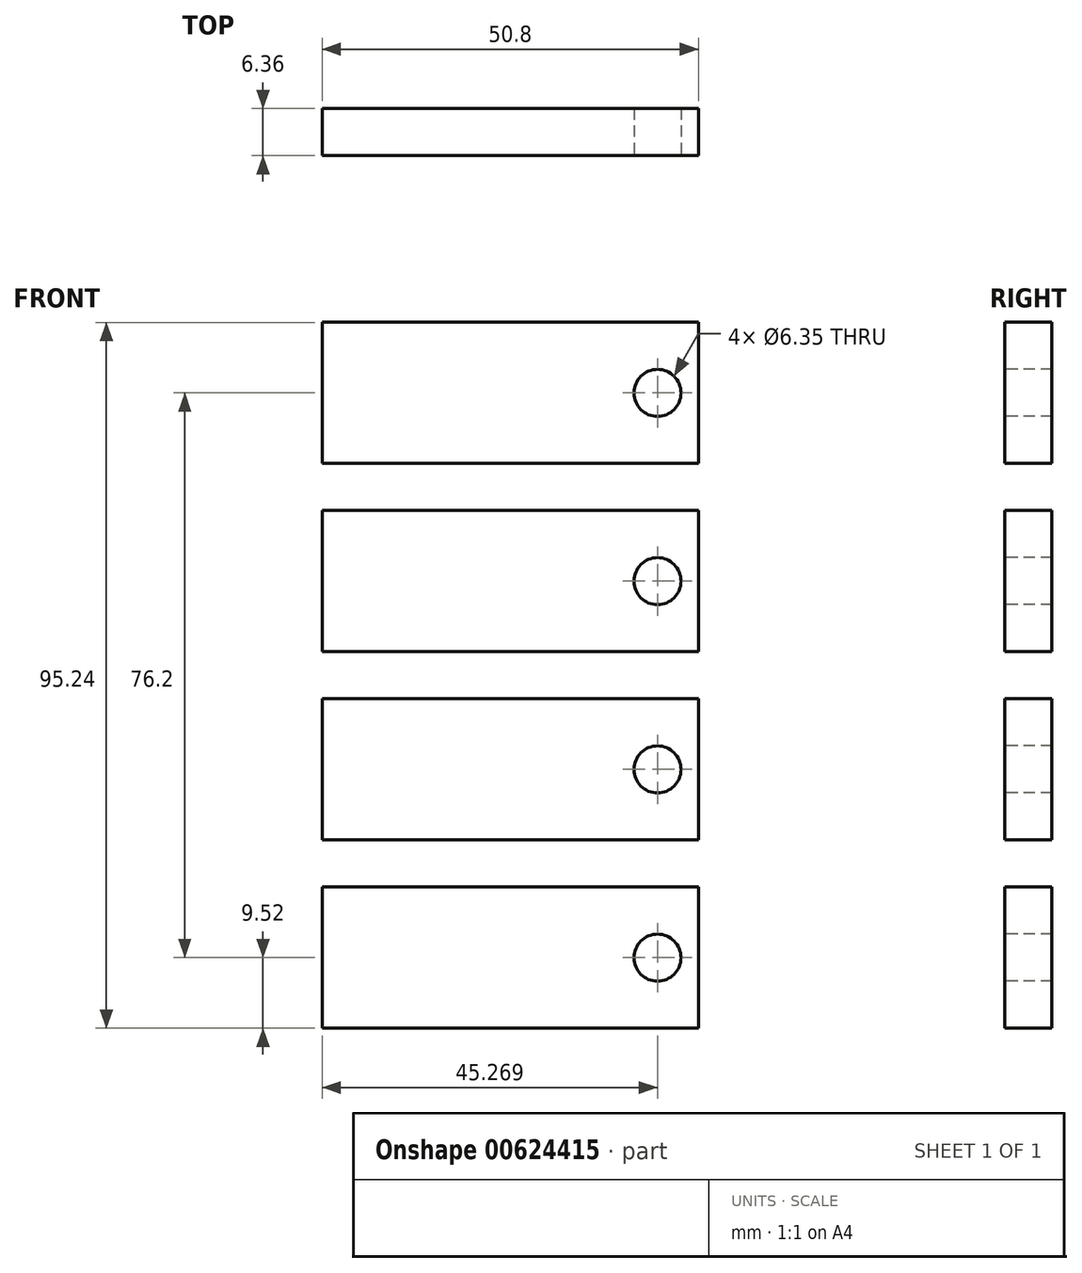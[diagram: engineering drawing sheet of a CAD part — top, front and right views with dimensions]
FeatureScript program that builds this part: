
annotation { "Feature Type Name" : "Feature", "Feature Type Description" : "" }
export const myFeature = defineFeature(function(context is Context, id is Id, definition is map)
    precondition{}
    {
        {
            var Q0;
            Q0=qCreatedBy(makeId("Front.planeOp"),FACE);
            var sketch = newSketch(context, id + "F0", { "sketchPlane" : qUnion([Q0])});
            skLineSegment(sketch, "E0.bottom", {"start": v(-25.4, -9.53) * mm, "end": v(25.4, -9.53) * mm});
            skLineSegment(sketch, "E0.top", {"start": v(-25.4, 9.53) * mm, "end": v(25.4, 9.53) * mm});
            skLineSegment(sketch, "E0.left", {"start": v(-25.4, -9.53) * mm, "end": v(-25.4, 9.53) * mm});
            skLineSegment(sketch, "E0.right", {"start": v(25.4, -9.53) * mm, "end": v(25.4, 9.53) * mm});
            skPoint(sketch, "E0.middle", {"position": v(0, 0) * mm});
            skLineSegment(sketch, "E1.bottom", {"start": v(-25.4, 15.88) * mm, "end": v(25.4, 15.88) * mm});
            skLineSegment(sketch, "E1.top", {"start": v(-25.4, 34.93) * mm, "end": v(25.4, 34.93) * mm});
            skLineSegment(sketch, "E1.left", {"start": v(-25.4, 15.88) * mm, "end": v(-25.4, 34.93) * mm});
            skLineSegment(sketch, "E1.right", {"start": v(25.4, 15.88) * mm, "end": v(25.4, 34.93) * mm});
            skPoint(sketch, "E1.middle", {"position": v(0, 25.4) * mm});
            skPoint(sketch, "E1.cornerSnap0", {"position": v(-25.4, 0) * mm});
            skLineSegment(sketch, "E2.bottom", {"start": v(-25.4, -34.92) * mm, "end": v(25.4, -34.92) * mm});
            skLineSegment(sketch, "E2.top", {"start": v(-25.4, -15.88) * mm, "end": v(25.4, -15.88) * mm});
            skLineSegment(sketch, "E2.left", {"start": v(-25.4, -34.93) * mm, "end": v(-25.4, -15.88) * mm});
            skLineSegment(sketch, "E2.right", {"start": v(25.4, -34.92) * mm, "end": v(25.4, -15.88) * mm});
            skPoint(sketch, "E2.middle", {"position": v(0, -25.4) * mm});
            skLineSegment(sketch, "E3.bottom", {"start": v(-25.4, -60.33) * mm, "end": v(25.4, -60.33) * mm});
            skLineSegment(sketch, "E3.top", {"start": v(-25.4, -41.28) * mm, "end": v(25.4, -41.28) * mm});
            skLineSegment(sketch, "E3.left", {"start": v(-25.4, -60.33) * mm, "end": v(-25.4, -41.28) * mm});
            skLineSegment(sketch, "E3.right", {"start": v(25.4, -60.33) * mm, "end": v(25.4, -41.28) * mm});
            skPoint(sketch, "E3.middle", {"position": v(0, -50.8) * mm});
            skSolve(sketch);
        }
        {
            var Q0;
            Q0 = qSketchRegion(id + "F0", true);
            extrude(context, id + "F1", {"entities" : qUnion([Q0]), "endBound" : BoundingType.SYMMETRIC, "depth" : 6.35 * mm, "offsetDistance" : 25.4 * mm});
        }
        {
            var Q0;
            Q0=makeQuery(id+"F1.opExtrude","CAP_FACE",FACE,{"disambiguationData":[OSD([sQuery(id+"F0.wireOp",EDGE,"E1.bottom"),sQuery(id+"F0.wireOp",EDGE,"E1.top"),sQuery(id+"F0.wireOp",EDGE,"E1.left"),sQuery(id+"F0.wireOp",EDGE,"E1.right")])],"isStart":false});
            var sketch = newSketch(context, id + "F2", { "sketchPlane" : qUnion([Q0])});
            skCircle(sketch, "E4", {"center": v(19.87, 25.4) * mm, "radius": 3.26 * mm});
            skPoint(sketch, "E4.centerSnap0", {"position": v(25.4, 25.4) * mm});
            skCircle(sketch, "E5", {"center": v(19.87, 0) * mm, "radius": 3.05 * mm});
            skCircle(sketch, "E6", {"center": v(19.87, -25.4) * mm, "radius": 3.05 * mm});
            skCircle(sketch, "E7", {"center": v(19.87, -50.8) * mm, "radius": 2.7 * mm});
            skSolve(sketch);
        }
        {
            var Q0;
            Q0=sQuery(id+"F2.wireOp",VERTEX,"E4.center");
            var Q1;
            Q1=sQuery(id+"F2.wireOp",VERTEX,"E5.center");
            var Q2;
            Q2=sQuery(id+"F2.wireOp",VERTEX,"E6.center");
            var Q3;
            Q3=sQuery(id+"F2.wireOp",VERTEX,"E7.center");
            var Q4;
            Q4=makeQuery(id+"F1.opExtrude","SWEPT_BODY",BODY,{"disambiguationData":[OSD([sQuery(id+"F0.wireOp",EDGE,"E1.bottom"),sQuery(id+"F0.wireOp",EDGE,"E1.top"),sQuery(id+"F0.wireOp",EDGE,"E1.left"),sQuery(id+"F0.wireOp",EDGE,"E1.right")])]});
            var Q5;
            Q5=makeQuery(id+"F1.opExtrude","SWEPT_BODY",BODY,{"disambiguationData":[OSD([sQuery(id+"F0.wireOp",EDGE,"E0.bottom"),sQuery(id+"F0.wireOp",EDGE,"E0.top"),sQuery(id+"F0.wireOp",EDGE,"E0.left"),sQuery(id+"F0.wireOp",EDGE,"E0.right")])]});
            var Q6;
            Q6=makeQuery(id+"F1.opExtrude","SWEPT_BODY",BODY,{"disambiguationData":[OSD([sQuery(id+"F0.wireOp",EDGE,"E2.bottom"),sQuery(id+"F0.wireOp",EDGE,"E2.top"),sQuery(id+"F0.wireOp",EDGE,"E2.left"),sQuery(id+"F0.wireOp",EDGE,"E2.right")])]});
            var Q7;
            Q7=makeQuery(id+"F1.opExtrude","SWEPT_BODY",BODY,{"disambiguationData":[OSD([sQuery(id+"F0.wireOp",EDGE,"E3.bottom"),sQuery(id+"F0.wireOp",EDGE,"E3.top"),sQuery(id+"F0.wireOp",EDGE,"E3.left"),sQuery(id+"F0.wireOp",EDGE,"E3.right")])]});
            hole(context, id + "F3", {"style" : HoleStyle.SIMPLE, "endStyle" : HoleEndStyle.THROUGH, "holeDiameter" : 6.35 * mm, "majorDiameter" : 6.35 * mm, "isTappedThrough" : true, "tappedDepth" : 12.7 * mm, "tapClearance" : 3, "locations" : qUnion([Q0, Q1, Q2, Q3]), "scope" : qUnion([Q4, Q5, Q6, Q7])});
        }
    });
